# Revit family: 2093111 Sylvania Lighting Fixture MC2-KIT D I 2-4M 3K DALI WHT PRIS
name_source: partatom
category: Lighting Fixtures
revit_build: Autodesk Revit 2016 (Build: 20150220_1215(x64)
units: mm (PartAtom-declared; Revit-internal decimal feet)

## family parameters
Cut with Voids When Loaded = No
Host = Face
Light Source = Yes
OmniClass Number = 23.80.70.11.17
OmniClass Title = Specialized Lighting by Location or Use
Part Type = Normal
Room Calculation Point = No
Round Connector Dimension = Use Diameter
Shared = No

## types (1)
- 2093111 MC2-KIT D/I 2.4M 3K DALI WHT PRIS
    Apparent Load = 64 VA
    Assembly Code = D5020200
    AssetType = Fixed
    Color Filter = 16777215
    Default Elevation = 0 mm  [stored 0 ft]
    Description = 2093111   MC2-KIT D/I 2.4M 3K DALI WHT PRIS  Continuous lines of LED light, white RAL 9016, direct/indirect distribution (65/35), suspended kit version is pre-wired and supplied complete with end caps and suspension cables, compact and minimalist design based on the Golden Mean, ideal for offices, meeting rooms, corridors, education facilities, museums and libraries, extruded aluminium body, diffuser: micro prismatic, colour temperature: 3000K warm white, total system power: 64W, total fixture output: 7392lm, luminaire efficacy: 116lm/W, LOR: 100%, colour rendering: Ra >80, LED Chromacity: 1 step MacAdam ellipse, lifetime: 60,000 hours at 90% of the original output (L90), energy class: A++, A+, A, IR/UV free light source without heat radiation, operating voltage: 220-240V / 50-60Hz, drive current: (Direct) 800mA + (Indirect) 350mA, electronic driver, DALI dimmable, direct/indirect independently addressable, electrical protection: CLASS I, IP20, suitable for internal environment only.
    Dimming Lamp Color Temperature Shift = <None>
    DocumentationLiterature = http://www.sylvania-lighting.com
    DurationUnit = hours
    ElectricShockClassification = Class I
    Emit Shape Visible in Rendering = No
    Emit from Rectangle Length = 2400 mm
    Emit from Rectangle Width = 52 mm  [stored 0.170604 ft]
    EndCapLeft_SYL = Yes
    EndCapRight_SYL = Yes
    ExpectedLife = 50000
    Height_SYL = 86 mm  [stored 0.282152 ft]
    IfcExportAs = IfcLightFixtureType
    IfcExportType = IfcLightFixtureType
    IngressProtection = IP20
    Keynote = 16500
    Lamp = LED
    LampColourRenderingIndex = 80
    LampColourTemperature = 3000 K
    LampMacAdamStep = 3
    LampNominalLuminous = 7392 lm
    LampsType = LED
    Length_SYL = 2400 mm
    LightOutputRatio = 100
    LuminousEfficacy = 116 lm/W
    Manufacturer = Feilo Sylvania
    ManufacturerName = Feilo Sylvania
    Material = aluminium housing, polycarbonate diffuser
    Material_1_SYL = Metal_Sylvania_Mini Continuum II_White
    Material_2_SYL = Polycarbonate_Sylvania_Mini Continuum II_Opal_4000K
    Material_3_SYL = Metal_Sylvania_Mini Contiuum II_Silver
    Material_4_SYL = Metal_Sylvania_Mini Contiuum II_Silver
    Model = MC2-KIT D/I 2.4M 3K DALI WHT PRIS
    ModelNumber = 2093111
    ModelReference = MC2-KIT D/I 2.4M 3K DALI WHT PRIS
    Name = MC2-KIT D/I 2.4M 3K DALI WHT PRIS
    NominalHeight = 86 mm  [stored 0.282152 ft]
    NominalLength = 2400 mm
    NominalWidth = 0 mm  [stored 0 ft]
    Photometric Web File = 2093111.ies
    PowerConsumption = 64 W
    PowerFactor = 0.95
    Tilt Angle = -90.00°
    TypeName = MC2-KIT D/I 2.4M 3K DALI WHT PRIS
    URL = http://www.sylvania-lighting.com
    Voltage = 0 V
    Weight = 6.5 kg
    Width_SYL = 54 mm  [stored 0.177165 ft]

note: [stored X ft] marks values corroborated as IEEE doubles in the binary element streams (Revit-internal decimal feet)

## geometry (parser evidence)
native form markers: Sweep x3
no freeform markers — native parametric forms only
